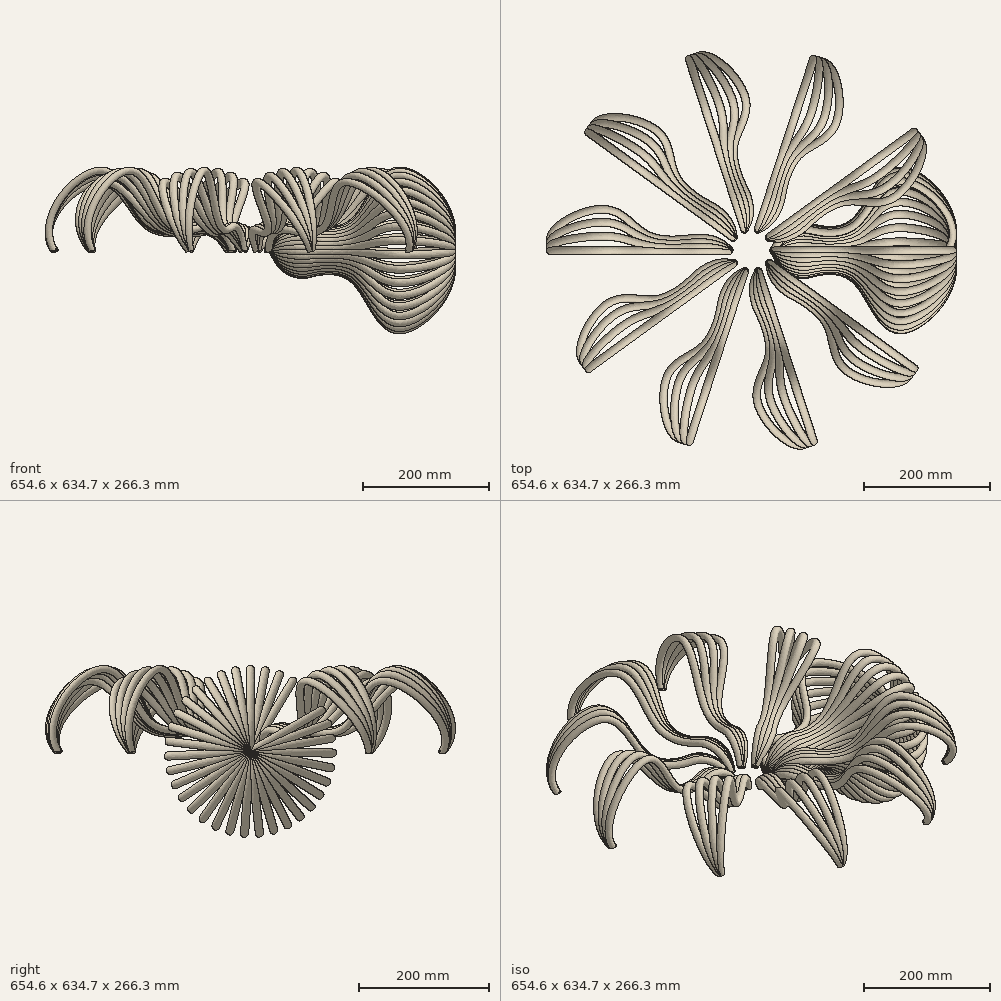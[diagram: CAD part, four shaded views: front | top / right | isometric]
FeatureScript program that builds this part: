
annotation { "Feature Type Name" : "Feature", "Feature Type Description" : "" }
export const myFeature = defineFeature(function(context is Context, id is Id, definition is map)
    precondition{}
    {
        {
            var Q0;
            Q0=qCreatedBy(makeId("Front.planeOp"),FACE);
            var sketch = newSketch(context, id + "F0", { "sketchPlane" : qUnion([Q0])});
            skFitSpline(sketch, "E0", {"points": [v(0, 0) * mm, v(17.7, 26.8) * mm, v(46.4, 39.01) * mm, v(70.97, 34.71) * mm, v(130.11, 47.43) * mm, v(202.43, 127.53) * mm, v(277.24, 0) * mm], "startDerivative": vector(98.4, 201.22) * mm, "endDerivative": vector(-377.25, -588.7) * mm});
            skSolve(sketch);
        }
        {
            var Q0;
            Q0=qCreatedBy(makeId("Top.planeOp"),FACE);
            var sketch = newSketch(context, id + "F1", { "sketchPlane" : qUnion([Q0])});
            skCircle(sketch, "E1", {"center": v(0, 0) * mm, "radius": 6.35 * mm});
            skSolve(sketch);
        }
        {
            var Q0;
            Q0=makeQuery(id+"F1.imprint","IMPRINT",FACE,{"disambiguationData":[TD([[makeQuery(id+"F1.imprint","IMPRINT",EDGE,{"derivedFrom":sQuery(id+"F1.wireOp",EDGE,"E1")}),1.0]])]});
            var Q1;
            Q1=sQuery(id+"F0.wireOp",EDGE,"E0");
            sweep(context, id + "F2", {"profiles" : qUnion([Q0]), "path" : qUnion([Q1])});
        }
        {
            var Q0;
            Q0=makeQuery(id+"F2.opSweep","CAP_FACE",FACE,{"disambiguationData":[OSD([sQuery(id+"F0.wireOp",VERTEX,"E0.end"),sQuery(id+"F1.wireOp",EDGE,"E1")])],"isStart":false});
            shell(context, id + "F3", {"entities" : qUnion([Q0]), "thickness" : 2.54 * mm});
        }
        {
            var Q0;
            Q0=qCreatedBy(makeId("Top.planeOp"),FACE);
            var sketch = newSketch(context, id + "F4", { "sketchPlane" : qUnion([Q0])});
            skLineSegment(sketch, "E2", {"start": v(0, 0) * mm, "end": v(95.74, 0) * mm});
            skSolve(sketch);
        }
        {
            var Q0;
            Q0=makeQuery(id+"F2.opSweep","SWEPT_BODY",BODY,{"disambiguationData":[OSD([sQuery(id+"F0.wireOp",EDGE,"E0"),sQuery(id+"F1.wireOp",EDGE,"E1")])]});
            var Q1;
            Q1=sQuery(id+"F4.wireOp",EDGE,"E2");
            circularPattern(context, id + "F5", {"entities" : qUnion([Q0]), "axis" : qUnion([Q1]), "angle" : 300 * degree, "instanceCount" : 30, "equalSpace" : true});
        }
        {
            var Q0;
            Q0=qCreatedBy(makeId("Front.planeOp"),FACE);
            var sketch = newSketch(context, id + "F6", { "sketchPlane" : qUnion([Q0])});
            skLineSegment(sketch, "E3", {"start": v(-35.6, -33.62) * mm, "end": v(-35.6, 143.2) * mm});
            skSolve(sketch);
        }
        {
            var Q0;
            Q0=makeQuery(id+"F2.opSweep","SWEPT_BODY",BODY,{"disambiguationData":[OSD([sQuery(id+"F0.wireOp",EDGE,"E0"),sQuery(id+"F1.wireOp",EDGE,"E1")])]});
            var Q1;
            Q1=makeQuery(id+"F5.opPattern","COPY",BODY,{"derivedFrom":makeQuery(id+"F2.opSweep","SWEPT_BODY",BODY,{"disambiguationData":[OSD([sQuery(id+"F0.wireOp",EDGE,"E0"),sQuery(id+"F1.wireOp",EDGE,"E1")])]}),"instanceName":"1"});
            var Q2;
            Q2=makeQuery(id+"F5.opPattern","COPY",BODY,{"derivedFrom":makeQuery(id+"F2.opSweep","SWEPT_BODY",BODY,{"disambiguationData":[OSD([sQuery(id+"F0.wireOp",EDGE,"E0"),sQuery(id+"F1.wireOp",EDGE,"E1")])]}),"instanceName":"2"});
            var Q3;
            Q3=makeQuery(id+"F5.opPattern","COPY",BODY,{"derivedFrom":makeQuery(id+"F2.opSweep","SWEPT_BODY",BODY,{"disambiguationData":[OSD([sQuery(id+"F0.wireOp",EDGE,"E0"),sQuery(id+"F1.wireOp",EDGE,"E1")])]}),"instanceName":"3"});
            var Q4;
            Q4=sQuery(id+"F6.wireOp",EDGE,"E3");
            circularPattern(context, id + "F7", {"entities" : qUnion([Q0, Q1, Q2, Q3]), "axis" : qUnion([Q4]), "angle" : 360 * degree, "instanceCount" : 10, "equalSpace" : true});
        }
    });
